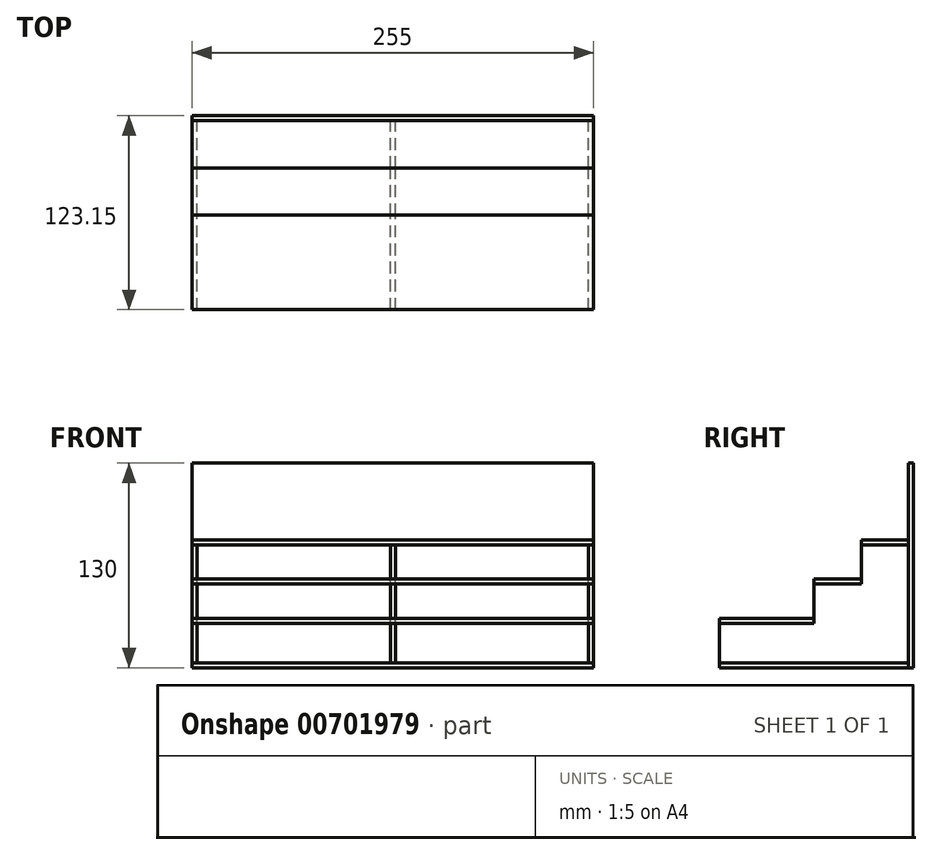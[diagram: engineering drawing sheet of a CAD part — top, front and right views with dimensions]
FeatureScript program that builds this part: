
annotation { "Feature Type Name" : "Feature", "Feature Type Description" : "" }
export const myFeature = defineFeature(function(context is Context, id is Id, definition is map)
    precondition{}
    {
        {
            assignVariable(context, id + "F0", {"name" : "x", "anyValue" : 3.15});
        }
        {
            var Q0;
            Q0=qCreatedBy(makeId("Top.planeOp"),FACE);
            var sketch = newSketch(context, id + "F1", { "sketchPlane" : qUnion([Q0])});
            skLineSegment(sketch, "E0.bottom", {"start": v(0, 0) * mm, "end": v(255, 0) * mm});
            skLineSegment(sketch, "E0.top", {"start": v(0, 120) * mm, "end": v(255, 120) * mm});
            skLineSegment(sketch, "E0.left", {"start": v(0, 0) * mm, "end": v(0, 120) * mm});
            skLineSegment(sketch, "E0.right", {"start": v(255, 0) * mm, "end": v(255, 120) * mm});
            skSolve(sketch);
        }
        {
            var Q0;
            Q0=qSketchRegion(id+"F1",true);
            extrude(context, id + "F2", {"entities" : qUnion([Q0]), "depth" : (getVariable(context, 'x')) * mm, "offsetDistance" : 25 * mm});
        }
        {
            var Q0;
            Q0=makeQuery(id+"F2.opExtrude","SWEPT_FACE",FACE,{"disambiguationData":[OSD([sQuery(id+"F1.wireOp",EDGE,"E0.left")])]});
            var sketch = newSketch(context, id + "F3", { "sketchPlane" : qUnion([Q0])});
            skLineSegment(sketch, "E1.left", {"start": v(0, 3.15) * mm, "end": v(0, 28.15) * mm});
            skLineSegment(sketch, "E2", {"start": v(0, 3.15) * mm, "end": v(-120, 3.15) * mm});
            skLineSegment(sketch, "E3", {"start": v(-120, 3.15) * mm, "end": v(-120, 78.15) * mm});
            skLineSegment(sketch, "E4", {"start": v(0, 28.15) * mm, "end": v(-60, 28.15) * mm});
            skLineSegment(sketch, "E5", {"start": v(-60, 28.15) * mm, "end": v(-60, 53.15) * mm});
            skLineSegment(sketch, "E6", {"start": v(-60, 53.15) * mm, "end": v(-90, 53.15) * mm});
            skLineSegment(sketch, "E7", {"start": v(-90, 53.15) * mm, "end": v(-90, 78.15) * mm});
            skLineSegment(sketch, "E8", {"start": v(-90, 78.15) * mm, "end": v(-120, 78.15) * mm});
            skLineSegment(sketch, "E9", {"start": v(-90, 53.15) * mm, "end": v(-90, 3.15) * mm, "construction": true});
            skLineSegment(sketch, "E10", {"start": v(-60, 28.15) * mm, "end": v(-90, 28.15) * mm, "construction": true});
            skSolve(sketch);
        }
        {
            var Q0;
            Q0=qSketchRegion(id+"F3",true);
            extrude(context, id + "F4", {"entities" : qUnion([Q0]), "oppositeDirection" : true, "depth" : (getVariable(context, 'x')) * mm, "offsetDistance" : 25 * mm});
        }
        {
            var Q0;
            Q0=makeQuery(id+"F4.opExtrude","SWEPT_BODY",BODY,{"disambiguationData":[OSD([sQuery(id+"F3.wireOp",EDGE,"E1.top"),sQuery(id+"F3.wireOp",EDGE,"E1.left"),sQuery(id+"F3.wireOp",EDGE,"E2"),sQuery(id+"F3.wireOp",EDGE,"E3")])]});
            transform(context, id + "F5", {"entities" : qUnion([Q0]), "transformType" : TransformType.TRANSLATION_3D, "dx" : (263.7 + 3.15 - 15) * mm, "dy" : 0 * mm, "dz" : 0 * mm, "makeCopy" : true});
        }
        {
            var Q0;
            Q0=makeQuery(id+"F4.opExtrude","SWEPT_BODY",BODY,{"disambiguationData":[OSD([sQuery(id+"F3.wireOp",EDGE,"E1.left"),sQuery(id+"F3.wireOp",EDGE,"E2"),sQuery(id+"F3.wireOp",EDGE,"E3"),sQuery(id+"F3.wireOp",EDGE,"E4"),sQuery(id+"F3.wireOp",EDGE,"E5"),sQuery(id+"F3.wireOp",EDGE,"E6"),sQuery(id+"F3.wireOp",EDGE,"E7"),sQuery(id+"F3.wireOp",EDGE,"E8")])]});
            transform(context, id + "F6", {"entities" : qUnion([Q0]), "transformType" : TransformType.TRANSLATION_3D, "dx" : 125.92 * mm, "dy" : 0 * mm, "dz" : 0 * mm, "makeCopy" : true});
        }
        {
            var Q0;
            Q0=makeQuery(id+"FVTuVMvbx6C6lcW_2.boolean.opBoolean","MERGE",FACE,{"derivedFrom":[makeQuery(id+"F4.opExtrude","SWEPT_FACE",FACE,{"disambiguationData":[OSD([sQuery(id+"F3.wireOp",EDGE,"E1.left")])]}),makeQuery(id+"FVTuVMvbx6C6lcW_2.opExtrude","SWEPT_FACE",FACE,{"disambiguationData":[OSD([sQuery(id+"F9WBSx8lvzqTq6O_2.wireOp",EDGE,"DdJYWYcg-8VXy-0sGO-iMAo-MInbchsGbsPU")])]})]});
            var sketch = newSketch(context, id + "F7", { "sketchPlane" : qUnion([Q0])});
            skLineSegment(sketch, "E11.bottom", {"start": v(0, 31.3) * mm, "end": v(255, 31.3) * mm});
            skLineSegment(sketch, "E11.top", {"start": v(0, 28.15) * mm, "end": v(255, 28.15) * mm});
            skLineSegment(sketch, "E11.right", {"start": v(255, 31.3) * mm, "end": v(255, 28.15) * mm});
            skLineSegment(sketch, "E12", {"start": v(0, 28.15) * mm, "end": v(0, 31.3) * mm});
            skSolve(sketch);
        }
        {
            var Q0;
            Q0=qSketchRegion(id+"F7",true);
            var Q1;
            Q1=makeQuery(id+"F5.opPattern","COPY",FACE,{"derivedFrom":makeQuery(id+"F4.opExtrude","SWEPT_FACE",FACE,{"disambiguationData":[OSD([sQuery(id+"F3.wireOp",EDGE,"E5")])]}),"instanceName":"1"});
            extrude(context, id + "F8", {"entities" : qUnion([Q0]), "endBound" : BoundingType.UP_TO_SURFACE, "oppositeDirection" : true, "depth" : 25 * mm, "endBoundEntityFace" : qUnion([Q1]), "offsetDistance" : 25 * mm});
        }
        {
            var Q0;
            Q0=makeQuery(id+"F4.opExtrude","SWEPT_FACE",FACE,{"disambiguationData":[OSD([sQuery(id+"F3.wireOp",EDGE,"E5")])]});
            var sketch = newSketch(context, id + "F9", { "sketchPlane" : qUnion([Q0])});
            skLineSegment(sketch, "E13.bottom", {"start": v(0, 53.15) * mm, "end": v(255, 53.15) * mm});
            skLineSegment(sketch, "E13.top", {"start": v(0, 56.3) * mm, "end": v(255, 56.3) * mm});
            skLineSegment(sketch, "E13.left", {"start": v(0, 53.15) * mm, "end": v(0, 56.3) * mm});
            skLineSegment(sketch, "E13.right", {"start": v(255, 53.15) * mm, "end": v(255, 56.3) * mm});
            skSolve(sketch);
        }
        {
            var Q0;
            Q0 = qSketchRegion(id + "F9", true);
            var Q1;
            Q1=makeQuery(id+"F4.opExtrude","SWEPT_FACE",FACE,{"disambiguationData":[OSD([sQuery(id+"F3.wireOp",EDGE,"E7")])]});
            extrude(context, id + "F10", {"entities" : qUnion([Q0]), "endBound" : BoundingType.UP_TO_SURFACE, "oppositeDirection" : true, "depth" : 25 * mm, "endBoundEntityFace" : qUnion([Q1]), "offsetDistance" : 25 * mm});
        }
        {
            var Q0;
            Q0=makeQuery(id+"F10.opExtrude","SWEPT_BODY",BODY,{"disambiguationData":[OSD([sQuery(id+"F9.wireOp",EDGE,"E13.bottom"),sQuery(id+"F9.wireOp",EDGE,"E13.top"),sQuery(id+"F9.wireOp",EDGE,"E13.left"),sQuery(id+"F9.wireOp",EDGE,"E13.right")])]});
            transform(context, id + "F11", {"entities" : qUnion([Q0]), "transformType" : TransformType.TRANSLATION_3D, "dx" : 0 * mm, "dy" : 30 * mm, "dz" : 25 * mm, "makeCopy" : true});
        }
        {
            var Q0;
            Q0=makeQuery(id+"F2.opExtrude","SWEPT_FACE",FACE,{"disambiguationData":[OSD([sQuery(id+"F1.wireOp",EDGE,"E0.top")])]});
            var sketch = newSketch(context, id + "F12", { "sketchPlane" : qUnion([Q0])});
            skLineSegment(sketch, "E14.bottom", {"start": v(-255, 130) * mm, "end": v(0, 130) * mm});
            skLineSegment(sketch, "E14.top", {"start": v(-255, 0) * mm, "end": v(0, 0) * mm});
            skLineSegment(sketch, "E14.left", {"start": v(-255, 130) * mm, "end": v(-255, 0) * mm});
            skLineSegment(sketch, "E14.right", {"start": v(0, 130) * mm, "end": v(0, 0) * mm});
            skSolve(sketch);
        }
        {
            var Q0;
            Q0=qSketchRegion(id+"F12",true);
            extrude(context, id + "F13", {"entities" : qUnion([Q0]), "depth" : (getVariable(context, 'x')) * mm, "offsetDistance" : 25 * mm});
        }
    });
